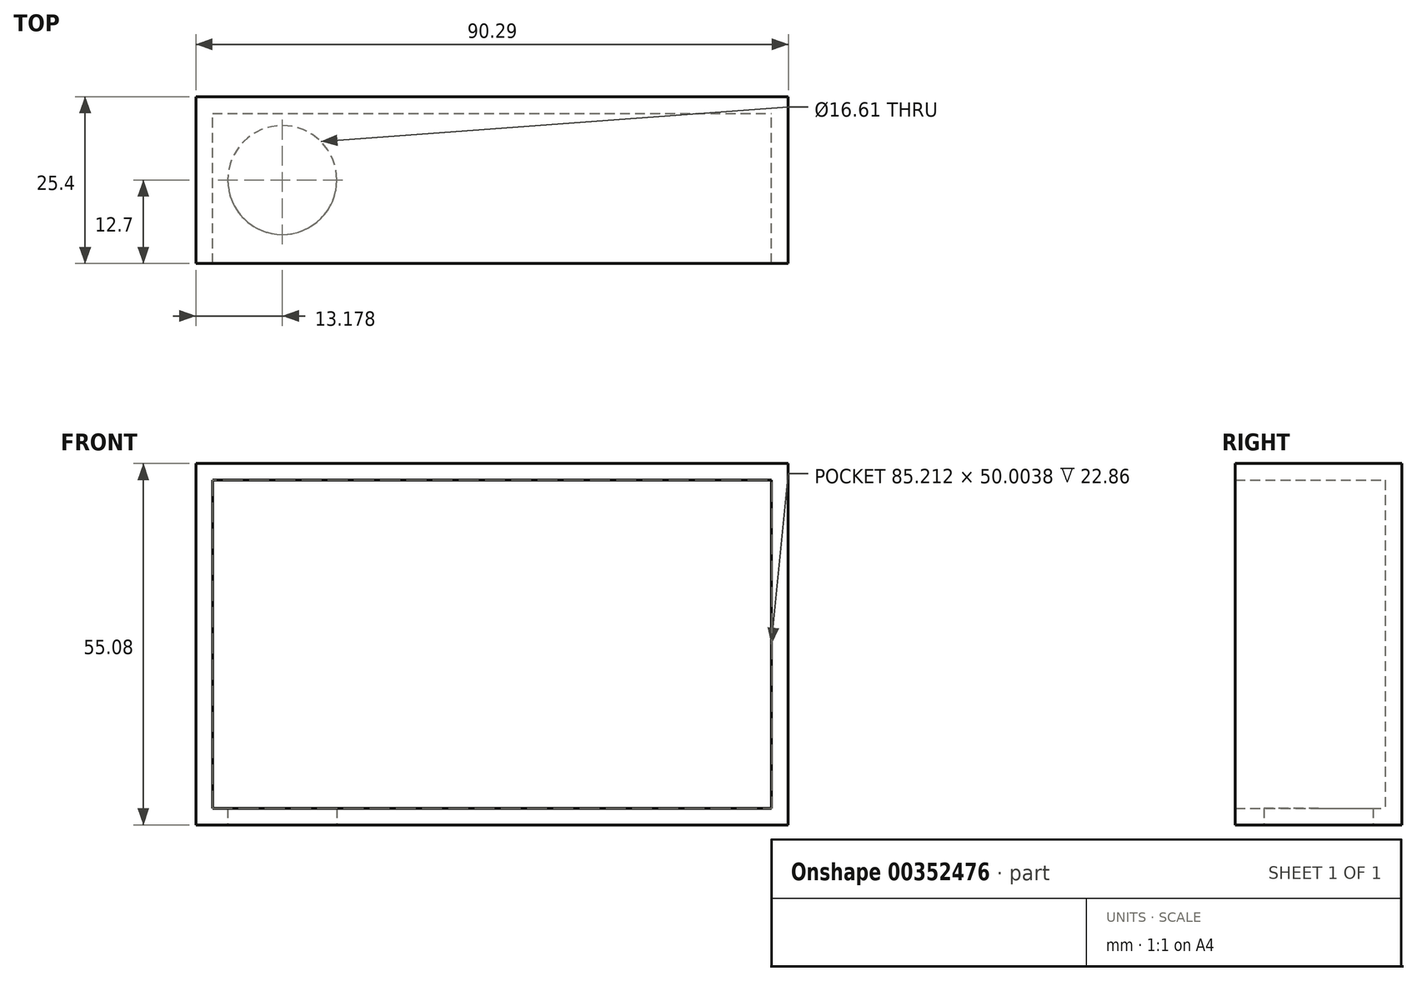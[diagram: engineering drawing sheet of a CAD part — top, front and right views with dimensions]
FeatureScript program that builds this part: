
annotation { "Feature Type Name" : "Feature", "Feature Type Description" : "" }
export const myFeature = defineFeature(function(context is Context, id is Id, definition is map)
    precondition{}
    {
        {
            var Q0;
            Q0=qCreatedBy(makeId("Front.planeOp"),FACE);
            var sketch = newSketch(context, id + "F0", { "sketchPlane" : qUnion([Q0])});
            skLineSegment(sketch, "E0.bottom", {"start": v(-40.6, 26.26) * mm, "end": v(49.69, 26.26) * mm});
            skLineSegment(sketch, "E0.top", {"start": v(-40.6, -28.82) * mm, "end": v(49.69, -28.82) * mm});
            skLineSegment(sketch, "E0.left", {"start": v(-40.6, 26.26) * mm, "end": v(-40.6, -28.82) * mm});
            skLineSegment(sketch, "E0.right", {"start": v(49.69, 26.26) * mm, "end": v(49.69, -28.82) * mm});
            skSolve(sketch);
        }
        {
            var Q0;
            Q0=makeQuery(id+"F0.imprint","IMPRINT",FACE,{"disambiguationData":[TD([[makeQuery(id+"F0.imprint","IMPRINT",EDGE,{"derivedFrom":sQuery(id+"F0.wireOp",EDGE,"E0.bottom")}),-1.0]])]});
            extrude(context, id + "F1", {"entities" : qUnion([Q0]), "endBound" : BoundingType.SYMMETRIC, "depth" : 25.4 * mm});
        }
        {
            var Q0;
            Q0=makeQuery(id+"F1.opExtrude","CAP_FACE",FACE,{"disambiguationData":[OSD([sQuery(id+"F0.wireOp",EDGE,"E0.bottom"),sQuery(id+"F0.wireOp",EDGE,"E0.top"),sQuery(id+"F0.wireOp",EDGE,"E0.left"),sQuery(id+"F0.wireOp",EDGE,"E0.right")])],"isStart":false});
            shell(context, id + "F2", {"entities" : qUnion([Q0]), "thickness" : 2.54 * mm});
        }
        {
            var Q0;
            Q0=makeQuery(id+"F1.opExtrude","SWEPT_FACE",FACE,{"disambiguationData":[OSD([sQuery(id+"F0.wireOp",EDGE,"E0.top")])]});
            var sketch = newSketch(context, id + "F3", { "sketchPlane" : qUnion([Q0])});
            skCircle(sketch, "E1", {"center": v(-27.42, 0) * mm, "radius": 8.3 * mm});
            skSolve(sketch);
        }
        {
            var Q0;
            Q0=makeQuery(id+"F3.imprint","IMPRINT",FACE,{"disambiguationData":[TD([[makeQuery(id+"F3.imprint","IMPRINT",EDGE,{"derivedFrom":sQuery(id+"F3.wireOp",EDGE,"E1")}),1.0]])]});
            extrude(context, id + "F4", {"entities" : qUnion([Q0]), "operationType" : NewBodyOperationType.REMOVE, "oppositeDirection" : true, "depth" : 25.4 * mm});
        }
    });
